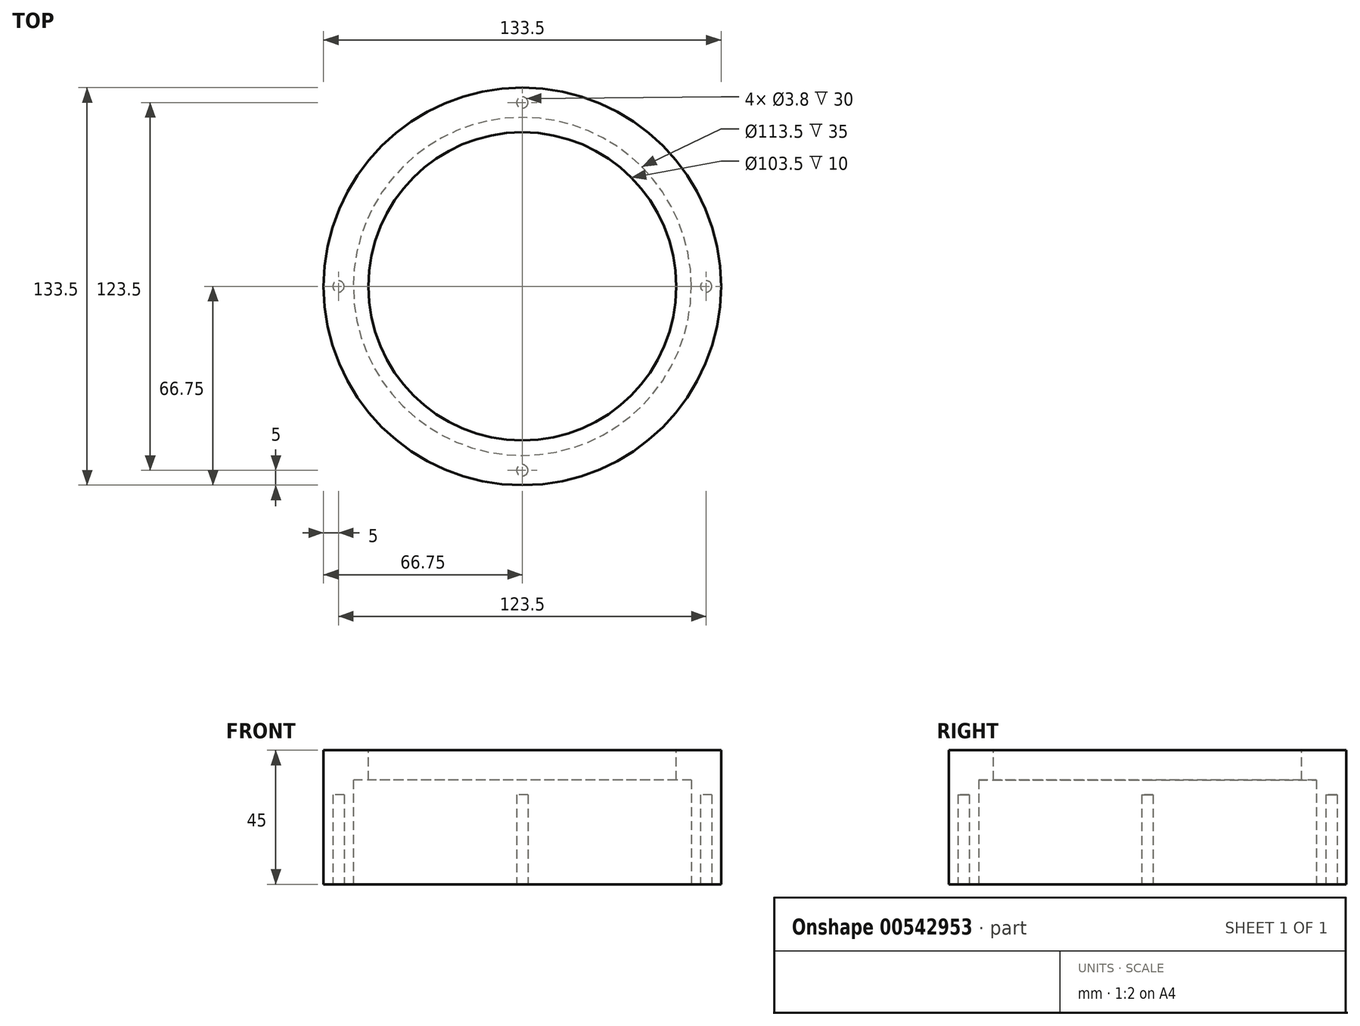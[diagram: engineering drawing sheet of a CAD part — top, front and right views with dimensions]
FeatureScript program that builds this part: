
annotation { "Feature Type Name" : "Feature", "Feature Type Description" : "" }
export const myFeature = defineFeature(function(context is Context, id is Id, definition is map)
    precondition{}
    {
        {
            var Q0;
            Q0=qCreatedBy(makeId("Top.planeOp"),FACE);
            var sketch = newSketch(context, id + "F0", { "sketchPlane" : qUnion([Q0])});
            skCircle(sketch, "E0", {"center": v(0, 0) * mm, "radius": 66.75 * mm});
            skCircle(sketch, "E1", {"center": v(0, 0) * mm, "radius": 56.75 * mm});
            skSolve(sketch);
        }
        {
            var Q0;
            Q0=makeQuery(id+"F0.imprint","IMPRINT",FACE,{"disambiguationData":[TD([[makeQuery(id+"F0.imprint","IMPRINT",EDGE,{"derivedFrom":sQuery(id+"F0.wireOp",EDGE,"E0")}),1.0]])]});
            extrude(context, id + "F1", {"entities" : qUnion([Q0]), "depth" : 45 * mm, "offsetDistance" : 25 * mm});
        }
        {
            var Q0;
            Q0=makeQuery(id+"F1.opExtrude","CAP_FACE",FACE,{"disambiguationData":[OSD([sQuery(id+"F0.wireOp",EDGE,"E0"),sQuery(id+"F0.wireOp",EDGE,"E1")])],"isStart":false});
            var sketch = newSketch(context, id + "F2", { "sketchPlane" : qUnion([Q0])});
            skCircle(sketch, "E2", {"center": v(0, 0) * mm, "radius": 66.75 * mm});
            skCircle(sketch, "E3", {"center": v(0, 0) * mm, "radius": 51.75 * mm});
            skSolve(sketch);
        }
        {
            var Q0;
            Q0=makeQuery(id+"F2.imprint","IMPRINT",FACE,{"disambiguationData":[TD([[makeQuery(id+"F2.imprint","IMPRINT",EDGE,{"derivedFrom":sQuery(id+"F2.wireOp",EDGE,"E3")}),-1.0]])]});
            var Q1;
            Q1=makeQuery(id+"F2.imprint","IMPRINT",FACE,{"disambiguationData":[TD([[makeQuery(id+"F2.imprint","IMPRINT",EDGE,{"derivedFrom":sQuery(id+"F2.wireOp",EDGE,"E2")}),1.0]])]});
            var Q2;
            Q2=sQuery(id+"F2.wireOp",EDGE,"E3");
            var Q3;
            Q3=sQuery(id+"F2.wireOp",EDGE,"E2");
            extrude(context, id + "F3", {"entities" : qUnion([Q0, Q1]), "operationType" : NewBodyOperationType.ADD, "surfaceEntities" : qUnion([Q2, Q3]), "oppositeDirection" : true, "depth" : 10 * mm, "offsetDistance" : 25 * mm});
        }
        {
            var Q0;
            Q0=qCreatedBy(makeId("Top.planeOp"),FACE);
            var sketch = newSketch(context, id + "F4", { "sketchPlane" : qUnion([Q0])});
            skCircle(sketch, "E4", {"center": v(0, 0) * mm, "radius": 61.75 * mm, "construction": true});
            skSolve(sketch);
        }
        {
            var Q0;
            Q0=qCreatedBy(makeId("Top.planeOp"),FACE);
            var sketch = newSketch(context, id + "F5", { "sketchPlane" : qUnion([Q0])});
            skCircle(sketch, "E5.0", {"center": v(0, 0) * mm, "radius": 61.75 * mm});
            skCircle(sketch, "E6", {"center": v(0, 61.75) * mm, "radius": 1.9 * mm});
            skCircle(sketch, "E7", {"center": v(-61.75, 0) * mm, "radius": 1.9 * mm});
            skCircle(sketch, "E8", {"center": v(0, -61.75) * mm, "radius": 1.9 * mm});
            skCircle(sketch, "E9", {"center": v(61.75, 0) * mm, "radius": 1.9 * mm});
            skSolve(sketch);
        }
        {
            var Q0;
            {var subQ0=sQuery(id+"F5.wireOp",EDGE,"E6");var subQ1=sQuery(id+"F5.wireOp",EDGE,"E5.0");var subQ2=makeQuery(id+"F5.imprint","INTERSECT",VERTEX,{"disambiguationData":[OD(0.0)],"derivedFrom":[subQ1,subQ0]});Q0=makeQuery(id+"F5.imprint","IMPRINT",FACE,{"disambiguationData":[TD([[makeQuery(id+"F5.imprint","IMPRINT",EDGE,{"disambiguationData":[TD([[subQ2,-1.0]])],"derivedFrom":subQ1}),-1.0]])]});}
            var Q1;
            {var subQ0=sQuery(id+"F5.wireOp",EDGE,"E6");var subQ1=sQuery(id+"F5.wireOp",EDGE,"E5.0");var subQ2=makeQuery(id+"F5.imprint","INTERSECT",VERTEX,{"disambiguationData":[OD(0.0)],"derivedFrom":[subQ1,subQ0]});Q1=makeQuery(id+"F5.imprint","IMPRINT",FACE,{"disambiguationData":[TD([[makeQuery(id+"F5.imprint","IMPRINT",EDGE,{"disambiguationData":[TD([[subQ2,-1.0]])],"derivedFrom":subQ1}),1.0]])]});}
            var Q2;
            {var subQ0=sQuery(id+"F5.wireOp",EDGE,"E9");var subQ1=sQuery(id+"F5.wireOp",EDGE,"E5.0");var subQ2=makeQuery(id+"F5.imprint","INTERSECT",VERTEX,{"disambiguationData":[OD(0.0)],"derivedFrom":[subQ1,subQ0]});Q2=makeQuery(id+"F5.imprint","IMPRINT",FACE,{"disambiguationData":[TD([[makeQuery(id+"F5.imprint","IMPRINT",EDGE,{"disambiguationData":[TD([[subQ2,1.0]])],"derivedFrom":subQ1}),-1.0]])]});}
            var Q3;
            {var subQ0=sQuery(id+"F5.wireOp",EDGE,"E9");var subQ1=sQuery(id+"F5.wireOp",EDGE,"E5.0");var subQ2=makeQuery(id+"F5.imprint","INTERSECT",VERTEX,{"disambiguationData":[OD(0.0)],"derivedFrom":[subQ1,subQ0]});Q3=makeQuery(id+"F5.imprint","IMPRINT",FACE,{"disambiguationData":[TD([[makeQuery(id+"F5.imprint","IMPRINT",EDGE,{"disambiguationData":[TD([[subQ2,1.0]])],"derivedFrom":subQ1}),1.0]])]});}
            var Q4;
            {var subQ0=sQuery(id+"F5.wireOp",EDGE,"E8");var subQ1=sQuery(id+"F5.wireOp",EDGE,"E5.0");var subQ2=makeQuery(id+"F5.imprint","INTERSECT",VERTEX,{"disambiguationData":[OD(0.0)],"derivedFrom":[subQ1,subQ0]});Q4=makeQuery(id+"F5.imprint","IMPRINT",FACE,{"disambiguationData":[TD([[makeQuery(id+"F5.imprint","IMPRINT",EDGE,{"disambiguationData":[TD([[subQ2,-1.0]])],"derivedFrom":subQ1}),-1.0]])]});}
            var Q5;
            {var subQ0=sQuery(id+"F5.wireOp",EDGE,"E8");var subQ1=sQuery(id+"F5.wireOp",EDGE,"E5.0");var subQ2=makeQuery(id+"F5.imprint","INTERSECT",VERTEX,{"disambiguationData":[OD(0.0)],"derivedFrom":[subQ1,subQ0]});Q5=makeQuery(id+"F5.imprint","IMPRINT",FACE,{"disambiguationData":[TD([[makeQuery(id+"F5.imprint","IMPRINT",EDGE,{"disambiguationData":[TD([[subQ2,-1.0]])],"derivedFrom":subQ1}),1.0]])]});}
            var Q6;
            {var subQ0=sQuery(id+"F5.wireOp",EDGE,"E7");var subQ1=sQuery(id+"F5.wireOp",EDGE,"E5.0");var subQ2=makeQuery(id+"F5.imprint","INTERSECT",VERTEX,{"disambiguationData":[OD(0.0)],"derivedFrom":[subQ1,subQ0]});Q6=makeQuery(id+"F5.imprint","IMPRINT",FACE,{"disambiguationData":[TD([[makeQuery(id+"F5.imprint","IMPRINT",EDGE,{"disambiguationData":[TD([[subQ2,-1.0]])],"derivedFrom":subQ1}),1.0]])]});}
            var Q7;
            {var subQ0=sQuery(id+"F5.wireOp",EDGE,"E7");var subQ1=sQuery(id+"F5.wireOp",EDGE,"E5.0");var subQ2=makeQuery(id+"F5.imprint","INTERSECT",VERTEX,{"disambiguationData":[OD(0.0)],"derivedFrom":[subQ1,subQ0]});Q7=makeQuery(id+"F5.imprint","IMPRINT",FACE,{"disambiguationData":[TD([[makeQuery(id+"F5.imprint","IMPRINT",EDGE,{"disambiguationData":[TD([[subQ2,-1.0]])],"derivedFrom":subQ1}),-1.0]])]});}
            extrude(context, id + "F6", {"entities" : qUnion([Q0, Q1, Q2, Q3, Q4, Q5, Q6, Q7]), "operationType" : NewBodyOperationType.REMOVE, "depth" : 30 * mm, "offsetDistance" : 25 * mm});
        }
    });
